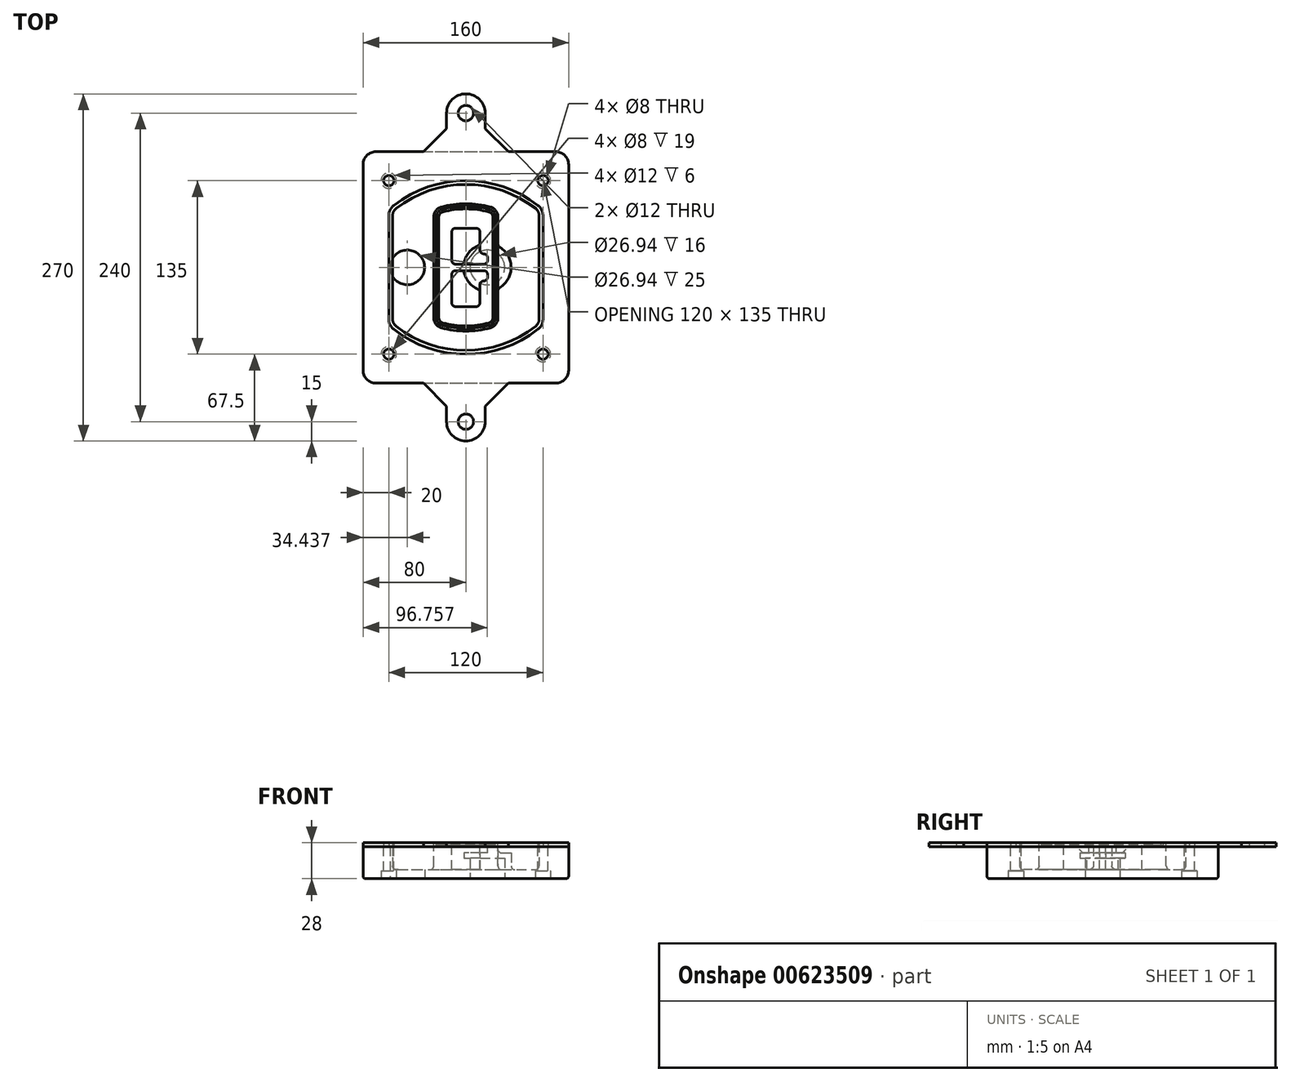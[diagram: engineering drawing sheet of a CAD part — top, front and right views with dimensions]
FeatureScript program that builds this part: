
annotation { "Feature Type Name" : "Feature", "Feature Type Description" : "" }
export const myFeature = defineFeature(function(context is Context, id is Id, definition is map)
    precondition{}
    {
        {
            var Q0;
            Q0=qCreatedBy(makeId("Top.planeOp"),FACE);
            var sketch = newSketch(context, id + "F0", { "sketchPlane" : qUnion([Q0])});
            skPoint(sketch, "E0.rect.middle", {"position": v(0, 0) * mm});
            skLineSegment(sketch, "E1.bottom", {"start": v(-70, -90) * mm, "end": v(70, -90) * mm});
            skLineSegment(sketch, "E1.top", {"start": v(-70, 90) * mm, "end": v(70, 90) * mm});
            skLineSegment(sketch, "E1.left", {"start": v(-80, -80) * mm, "end": v(-80, 80) * mm});
            skLineSegment(sketch, "E1.right", {"start": v(80, -80) * mm, "end": v(80, 80) * mm});
            skLineSegment(sketch, "E2", {"start": v(-80, 90) * mm, "end": v(80, -90) * mm, "construction": true});
            skLineSegment(sketch, "E3", {"start": v(80, 90) * mm, "end": v(-80, -90) * mm, "construction": true});
            skCircle(sketch, "E4", {"center": v(-60, 67.5) * mm, "radius": 4 * mm});
            skCircle(sketch, "E5", {"center": v(60, 67.5) * mm, "radius": 4 * mm});
            skCircle(sketch, "E6", {"center": v(60, -67.5) * mm, "radius": 4 * mm});
            skCircle(sketch, "E7", {"center": v(-60, -67.5) * mm, "radius": 4 * mm});
            skLineSegment(sketch, "E8", {"start": v(-60, 67.5) * mm, "end": v(60, 67.5) * mm, "construction": true});
            skLineSegment(sketch, "E9", {"start": v(60, 67.5) * mm, "end": v(60, -67.5) * mm, "construction": true});
            skLineSegment(sketch, "E10", {"start": v(60, -67.5) * mm, "end": v(-60, -67.5) * mm, "construction": true});
            skLineSegment(sketch, "E11", {"start": v(-60, -67.5) * mm, "end": v(-60, 67.5) * mm, "construction": true});
            skLineSegment(sketch, "E12", {"start": v(-60, 40.3) * mm, "end": v(-60, -40.3) * mm});
            skLineSegment(sketch, "E13", {"start": v(60, 40.3) * mm, "end": v(60, -40.3) * mm});
            skArc(sketch, "E14", {"start": v(56.15, 48.18) * mm, "mid": v(0, 67.5) * mm, "end": v(-56.15, 48.18) * mm});
            skArc(sketch, "E15", {"start": v(-56.15, -48.18) * mm, "mid": v(0, -67.5) * mm, "end": v(56.15, -48.18) * mm});
            skLineSegment(sketch, "E16", {"start": v(-60, 0) * mm, "end": v(60, 0) * mm, "construction": true});
            skPoint(sketch, "E17.visualSharp", {"position": v(-60, -45) * mm});
            skArc(sketch, "E17.filletArc", {"start": v(-60, -40.3) * mm, "mid": v(-58.99, -44.68) * mm, "end": v(-56.15, -48.18) * mm});
            skPoint(sketch, "E18.visualSharp", {"position": v(-60, 45) * mm});
            skArc(sketch, "E18.filletArc", {"start": v(-56.15, 48.18) * mm, "mid": v(-58.99, 44.68) * mm, "end": v(-60, 40.3) * mm});
            skPoint(sketch, "E19.visualSharp", {"position": v(60, 45) * mm});
            skArc(sketch, "E19.filletArc", {"start": v(60, 40.3) * mm, "mid": v(58.99, 44.68) * mm, "end": v(56.15, 48.18) * mm});
            skPoint(sketch, "E20.visualSharp", {"position": v(60, -45) * mm});
            skArc(sketch, "E20.filletArc", {"start": v(56.15, -48.18) * mm, "mid": v(58.99, -44.68) * mm, "end": v(60, -40.3) * mm});
            skPoint(sketch, "E21.visualSharp", {"position": v(-80, 90) * mm});
            skArc(sketch, "E21.filletArc", {"start": v(-70, 90) * mm, "mid": v(-77.07, 87.07) * mm, "end": v(-80, 80) * mm});
            skPoint(sketch, "E22.visualSharp", {"position": v(80, 90) * mm});
            skArc(sketch, "E22.filletArc", {"start": v(80, 80) * mm, "mid": v(77.07, 87.07) * mm, "end": v(70, 90) * mm});
            skPoint(sketch, "E23.visualSharp", {"position": v(80, -90) * mm});
            skArc(sketch, "E23.filletArc", {"start": v(70, -90) * mm, "mid": v(77.07, -87.07) * mm, "end": v(80, -80) * mm});
            skPoint(sketch, "E24.visualSharp", {"position": v(-80, -90) * mm});
            skArc(sketch, "E24.filletArc", {"start": v(-80, -80) * mm, "mid": v(-77.07, -87.07) * mm, "end": v(-70, -90) * mm});
            skArc(sketch, "E25.0", {"start": v(57, 40.3) * mm, "mid": v(56.3, 43.36) * mm, "end": v(54.3, 45.81) * mm});
            skLineSegment(sketch, "E25.1", {"start": v(57, 40.3) * mm, "end": v(57, -40.3) * mm});
            skArc(sketch, "E25.2", {"start": v(54.3, -45.81) * mm, "mid": v(56.3, -43.36) * mm, "end": v(57, -40.3) * mm});
            skArc(sketch, "E25.3", {"start": v(-54.3, -45.81) * mm, "mid": v(0, -64.5) * mm, "end": v(54.3, -45.81) * mm});
            skArc(sketch, "E25.4", {"start": v(-57, -40.3) * mm, "mid": v(-56.3, -43.36) * mm, "end": v(-54.3, -45.81) * mm});
            skArc(sketch, "E25.5", {"start": v(54.3, 45.81) * mm, "mid": v(0, 64.5) * mm, "end": v(-54.3, 45.81) * mm});
            skLineSegment(sketch, "E25.6", {"start": v(-57, 40.3) * mm, "end": v(-57, -40.3) * mm});
            skArc(sketch, "E25.7", {"start": v(-54.3, 45.81) * mm, "mid": v(-56.3, 43.36) * mm, "end": v(-57, 40.3) * mm});
            skArc(sketch, "E26.0", {"start": v(-58.62, 51.33) * mm, "mid": v(-62.58, 46.43) * mm, "end": v(-64, 40.3) * mm});
            skArc(sketch, "E26.1", {"start": v(58.62, 51.33) * mm, "mid": v(0, 71.5) * mm, "end": v(-58.62, 51.33) * mm});
            skArc(sketch, "E26.2", {"start": v(64, 40.3) * mm, "mid": v(62.58, 46.43) * mm, "end": v(58.62, 51.33) * mm});
            skLineSegment(sketch, "E26.3", {"start": v(64, 40.3) * mm, "end": v(64, -40.3) * mm});
            skArc(sketch, "E26.4", {"start": v(58.62, -51.33) * mm, "mid": v(62.58, -46.43) * mm, "end": v(64, -40.3) * mm});
            skLineSegment(sketch, "E26.5", {"start": v(-64, 40.3) * mm, "end": v(-64, -40.3) * mm});
            skArc(sketch, "E26.6", {"start": v(-58.62, -51.33) * mm, "mid": v(0, -71.5) * mm, "end": v(58.62, -51.33) * mm});
            skArc(sketch, "E26.7", {"start": v(-64, -40.3) * mm, "mid": v(-62.58, -46.43) * mm, "end": v(-58.62, -51.33) * mm});
            skSolve(sketch);
        }
        {
            var Q0;
            Q0=makeQuery(id+"F0.imprint","IMPRINT",FACE,{"disambiguationData":[TD([[makeQuery(id+"F0.imprint","IMPRINT",EDGE,{"derivedFrom":sQuery(id+"F0.wireOp",EDGE,"E1.bottom")}),1.0]])]});
            var Q1;
            Q1=makeQuery(id+"F0.imprint","IMPRINT",FACE,{"disambiguationData":[TD([[makeQuery(id+"F0.imprint","IMPRINT",EDGE,{"derivedFrom":sQuery(id+"F0.wireOp",EDGE,"E12")}),1.0]])]});
            var Q2;
            Q2=makeQuery(id+"F0.imprint","IMPRINT",FACE,{"disambiguationData":[TD([[makeQuery(id+"F0.imprint","IMPRINT",EDGE,{"derivedFrom":sQuery(id+"F0.wireOp",EDGE,"E25.0")}),1.0]])]});
            var Q3;
            Q3=makeQuery(id+"F0.imprint","IMPRINT",FACE,{"disambiguationData":[TD([[makeQuery(id+"F0.imprint","IMPRINT",EDGE,{"derivedFrom":sQuery(id+"F0.wireOp",EDGE,"E12")}),-1.0]])]});
            extrude(context, id + "F1", {"entities" : qUnion([Q0, Q1, Q2, Q3]), "oppositeDirection" : true, "depth" : 25 * mm});
        }
        {
            var Q0;
            Q0=makeQuery(id+"F0.imprint","IMPRINT",FACE,{"disambiguationData":[TD([[makeQuery(id+"F0.imprint","IMPRINT",EDGE,{"derivedFrom":sQuery(id+"F0.wireOp",EDGE,"E12")}),1.0]])]});
            extrude(context, id + "F2", {"entities" : qUnion([Q0]), "operationType" : NewBodyOperationType.ADD, "depth" : 3 * mm});
        }
        {
            var Q0;
            Q0=makeQuery(id+"F0.imprint","IMPRINT",FACE,{"disambiguationData":[TD([[makeQuery(id+"F0.imprint","IMPRINT",EDGE,{"derivedFrom":sQuery(id+"F0.wireOp",EDGE,"E25.0")}),1.0]])]});
            extrude(context, id + "F3", {"entities" : qUnion([Q0]), "operationType" : NewBodyOperationType.REMOVE, "oppositeDirection" : true, "depth" : 18 * mm});
        }
        {
            var Q0;
            Q0=makeQuery(id+"F2.opExtrude","CAP_FACE",FACE,{"disambiguationData":[OSD([sQuery(id+"F0.wireOp",EDGE,"E12"),sQuery(id+"F0.wireOp",EDGE,"E13"),sQuery(id+"F0.wireOp",EDGE,"E14"),sQuery(id+"F0.wireOp",EDGE,"E15"),sQuery(id+"F0.wireOp",EDGE,"E17.filletArc"),sQuery(id+"F0.wireOp",EDGE,"E18.filletArc"),sQuery(id+"F0.wireOp",EDGE,"E19.filletArc"),sQuery(id+"F0.wireOp",EDGE,"E20.filletArc"),sQuery(id+"F0.wireOp",EDGE,"E25.0"),sQuery(id+"F0.wireOp",EDGE,"E25.1"),sQuery(id+"F0.wireOp",EDGE,"E25.2"),sQuery(id+"F0.wireOp",EDGE,"E25.3"),sQuery(id+"F0.wireOp",EDGE,"E25.4"),sQuery(id+"F0.wireOp",EDGE,"E25.5"),sQuery(id+"F0.wireOp",EDGE,"E25.6"),sQuery(id+"F0.wireOp",EDGE,"E25.7")])],"isStart":false});
            var sketch = newSketch(context, id + "F4", { "sketchPlane" : qUnion([Q0])});
            skArc(sketch, "E27.0", {"start": v(-19.08, -46.97) * mm, "mid": v(0, -49.5) * mm, "end": v(19.08, -46.97) * mm});
            skArc(sketch, "E28.0", {"start": v(19.08, 46.97) * mm, "mid": v(0, 49.5) * mm, "end": v(-19.08, 46.97) * mm});
            skLineSegment(sketch, "E29", {"start": v(-25, 39.25) * mm, "end": v(-25, -39.25) * mm});
            skLineSegment(sketch, "E30", {"start": v(25, 39.25) * mm, "end": v(25, -39.25) * mm});
            skLineSegment(sketch, "E31", {"start": v(-25, 45.1) * mm, "end": v(25, 45.1) * mm, "construction": true});
            skLineSegment(sketch, "E32", {"start": v(-25, -45.1) * mm, "end": v(25, -45.1) * mm, "construction": true});
            skPoint(sketch, "E33.visualSharp", {"position": v(-25, 45.1) * mm});
            skArc(sketch, "E33.filletArc", {"start": v(-19.08, 46.97) * mm, "mid": v(-23.35, 44.11) * mm, "end": v(-25, 39.25) * mm});
            skPoint(sketch, "E34.visualSharp", {"position": v(25, 45.1) * mm});
            skArc(sketch, "E34.filletArc", {"start": v(25, 39.25) * mm, "mid": v(23.35, 44.11) * mm, "end": v(19.08, 46.97) * mm});
            skPoint(sketch, "E35.visualSharp", {"position": v(25, -45.1) * mm});
            skArc(sketch, "E35.filletArc", {"start": v(19.08, -46.97) * mm, "mid": v(23.35, -44.11) * mm, "end": v(25, -39.25) * mm});
            skPoint(sketch, "E36.visualSharp", {"position": v(-25, -45.1) * mm});
            skArc(sketch, "E36.filletArc", {"start": v(-25, -39.25) * mm, "mid": v(-23.35, -44.11) * mm, "end": v(-19.08, -46.97) * mm});
            skArc(sketch, "E37.0", {"start": v(54.3, 45.81) * mm, "mid": v(0, 64.5) * mm, "end": v(-54.3, 45.81) * mm});
            skArc(sketch, "E37.1", {"start": v(-54.3, 45.81) * mm, "mid": v(-56.3, 43.36) * mm, "end": v(-57, 40.3) * mm});
            skLineSegment(sketch, "E37.2", {"start": v(-57, 40.3) * mm, "end": v(-57, -40.3) * mm});
            skArc(sketch, "E37.3", {"start": v(-57, -40.3) * mm, "mid": v(-56.3, -43.36) * mm, "end": v(-54.3, -45.81) * mm});
            skArc(sketch, "E37.4", {"start": v(-54.3, -45.81) * mm, "mid": v(0, -64.5) * mm, "end": v(54.3, -45.81) * mm});
            skArc(sketch, "E37.5", {"start": v(54.3, -45.81) * mm, "mid": v(56.3, -43.36) * mm, "end": v(57, -40.3) * mm});
            skLineSegment(sketch, "E37.6", {"start": v(57, 40.3) * mm, "end": v(57, -40.3) * mm});
            skArc(sketch, "E37.7", {"start": v(57, 40.3) * mm, "mid": v(56.3, 43.36) * mm, "end": v(54.3, 45.81) * mm});
            skLineSegment(sketch, "E38.0", {"start": v(23, 39.25) * mm, "end": v(23, -39.25) * mm});
            skArc(sketch, "E38.1", {"start": v(18.56, -45.04) * mm, "mid": v(21.76, -42.9) * mm, "end": v(23, -39.25) * mm});
            skArc(sketch, "E38.2", {"start": v(-18.56, -45.04) * mm, "mid": v(0, -47.5) * mm, "end": v(18.56, -45.04) * mm});
            skArc(sketch, "E38.3", {"start": v(-23, -39.25) * mm, "mid": v(-21.76, -42.9) * mm, "end": v(-18.56, -45.04) * mm});
            skLineSegment(sketch, "E38.4", {"start": v(-23, 39.25) * mm, "end": v(-23, -39.25) * mm});
            skArc(sketch, "E38.5", {"start": v(23, 39.25) * mm, "mid": v(21.76, 42.9) * mm, "end": v(18.56, 45.04) * mm});
            skArc(sketch, "E38.6", {"start": v(-18.56, 45.04) * mm, "mid": v(-21.76, 42.9) * mm, "end": v(-23, 39.25) * mm});
            skArc(sketch, "E38.7", {"start": v(18.56, 45.04) * mm, "mid": v(0, 47.5) * mm, "end": v(-18.56, 45.04) * mm});
            skArc(sketch, "E39.0", {"start": v(21, 39.25) * mm, "mid": v(20.18, 41.68) * mm, "end": v(18.04, 43.1) * mm});
            skLineSegment(sketch, "E39.1", {"start": v(21, 39.25) * mm, "end": v(21, -39.25) * mm});
            skArc(sketch, "E39.2", {"start": v(18.04, -43.1) * mm, "mid": v(20.18, -41.68) * mm, "end": v(21, -39.25) * mm});
            skArc(sketch, "E39.3", {"start": v(-18.04, -43.1) * mm, "mid": v(0, -45.5) * mm, "end": v(18.04, -43.1) * mm});
            skArc(sketch, "E39.4", {"start": v(-21, -39.25) * mm, "mid": v(-20.18, -41.68) * mm, "end": v(-18.04, -43.1) * mm});
            skArc(sketch, "E39.5", {"start": v(18.04, 43.1) * mm, "mid": v(0, 45.5) * mm, "end": v(-18.04, 43.1) * mm});
            skLineSegment(sketch, "E39.6", {"start": v(-21, 39.25) * mm, "end": v(-21, -39.25) * mm});
            skArc(sketch, "E39.7", {"start": v(-18.04, 43.1) * mm, "mid": v(-20.18, 41.68) * mm, "end": v(-21, 39.25) * mm});
            skLineSegment(sketch, "E40", {"start": v(-25, 0) * mm, "end": v(25, 0) * mm, "construction": true});
            skLineSegment(sketch, "E41", {"start": v(-11, 5.5) * mm, "end": v(-11, 27.5) * mm});
            skLineSegment(sketch, "E42", {"start": v(-8, 30.5) * mm, "end": v(8, 30.5) * mm});
            skLineSegment(sketch, "E43", {"start": v(11, 27.5) * mm, "end": v(11, 13.5) * mm});
            skLineSegment(sketch, "E44", {"start": v(14, 10.5) * mm, "end": v(14, 10.5) * mm});
            skLineSegment(sketch, "E45", {"start": v(17, 7.5) * mm, "end": v(17, 5.5) * mm});
            skLineSegment(sketch, "E46", {"start": v(14, 2.5) * mm, "end": v(-8, 2.5) * mm});
            skPoint(sketch, "E47.visualSharp", {"position": v(-11, 30.5) * mm});
            skArc(sketch, "E47.filletArc", {"start": v(-8, 30.5) * mm, "mid": v(-10.12, 29.62) * mm, "end": v(-11, 27.5) * mm});
            skPoint(sketch, "E48.visualSharp", {"position": v(11, 30.5) * mm});
            skArc(sketch, "E48.filletArc", {"start": v(11, 27.5) * mm, "mid": v(10.12, 29.62) * mm, "end": v(8, 30.5) * mm});
            skPoint(sketch, "E49.visualSharp", {"position": v(11, 10.5) * mm});
            skArc(sketch, "E49.filletArc", {"start": v(11, 13.5) * mm, "mid": v(11.88, 11.38) * mm, "end": v(14, 10.5) * mm});
            skPoint(sketch, "E50.visualSharp", {"position": v(17, 10.5) * mm});
            skArc(sketch, "E50.filletArc", {"start": v(17, 7.5) * mm, "mid": v(16.12, 9.62) * mm, "end": v(14, 10.5) * mm});
            skPoint(sketch, "E51.visualSharp", {"position": v(17, 2.5) * mm});
            skArc(sketch, "E51.filletArc", {"start": v(14, 2.5) * mm, "mid": v(16.12, 3.38) * mm, "end": v(17, 5.5) * mm});
            skPoint(sketch, "E52.visualSharp", {"position": v(-11, 2.5) * mm});
            skArc(sketch, "E52.filletArc", {"start": v(-11, 5.5) * mm, "mid": v(-10.12, 3.38) * mm, "end": v(-8, 2.5) * mm});
            skLineSegment(sketch, "E53.0.MirrorCS", {"start": v(14, -2.5) * mm, "end": v(-8, -2.5) * mm});
            skArc(sketch, "E54.0.MirrorCS", {"start": v(-11, -5.5) * mm, "mid": v(-10.12, -3.38) * mm, "end": v(-8, -2.5) * mm});
            skLineSegment(sketch, "E55.0.MirrorCS", {"start": v(-11, -5.5) * mm, "end": v(-11, -27.5) * mm});
            skArc(sketch, "E56.0.MirrorCS", {"start": v(-8, -30.5) * mm, "mid": v(-10.12, -29.62) * mm, "end": v(-11, -27.5) * mm});
            skLineSegment(sketch, "E57.0.MirrorCS", {"start": v(-8, -30.5) * mm, "end": v(8, -30.5) * mm});
            skArc(sketch, "E58.0.MirrorCS", {"start": v(11, -27.5) * mm, "mid": v(10.12, -29.62) * mm, "end": v(8, -30.5) * mm});
            skLineSegment(sketch, "E59.0.MirrorCS", {"start": v(11, -27.5) * mm, "end": v(11, -13.5) * mm});
            skArc(sketch, "E60.0.MirrorCS", {"start": v(11, -13.5) * mm, "mid": v(11.88, -11.38) * mm, "end": v(14, -10.5) * mm});
            skArc(sketch, "E61.0.MirrorCS", {"start": v(17, -7.5) * mm, "mid": v(16.12, -9.62) * mm, "end": v(14, -10.5) * mm});
            skLineSegment(sketch, "E62.0.MirrorCS", {"start": v(17, -7.5) * mm, "end": v(17, -5.5) * mm});
            skArc(sketch, "E63.0.MirrorCS", {"start": v(14, -2.5) * mm, "mid": v(16.12, -3.38) * mm, "end": v(17, -5.5) * mm});
            skSolve(sketch);
        }
        {
            var Q0;
            Q0=makeQuery(id+"F4.imprint","IMPRINT",FACE,{"disambiguationData":[TD([[makeQuery(id+"F4.imprint","IMPRINT",EDGE,{"derivedFrom":sQuery(id+"F4.wireOp",EDGE,"E27.0")}),1.0]])]});
            var Q1;
            Q1=makeQuery(id+"F4.imprint","IMPRINT",FACE,{"disambiguationData":[TD([[makeQuery(id+"F4.imprint","IMPRINT",EDGE,{"derivedFrom":sQuery(id+"F4.wireOp",EDGE,"E38.0")}),-1.0]])]});
            var Q2;
            Q2=makeQuery(id+"F4.imprint","IMPRINT",FACE,{"disambiguationData":[TD([[makeQuery(id+"F4.imprint","IMPRINT",EDGE,{"derivedFrom":sQuery(id+"F4.wireOp",EDGE,"E39.0")}),1.0]])]});
            extrude(context, id + "F5", {"entities" : qUnion([Q0, Q1, Q2]), "operationType" : NewBodyOperationType.ADD, "endBound" : BoundingType.UP_TO_NEXT, "oppositeDirection" : true, "depth" : 25 * mm});
        }
        {
            var Q0;
            Q0=makeQuery(id+"F4.imprint","IMPRINT",FACE,{"disambiguationData":[TD([[makeQuery(id+"F4.imprint","IMPRINT",EDGE,{"derivedFrom":sQuery(id+"F4.wireOp",EDGE,"E38.0")}),-1.0]])]});
            extrude(context, id + "F6", {"entities" : qUnion([Q0]), "operationType" : NewBodyOperationType.REMOVE, "oppositeDirection" : true, "depth" : 2 * mm});
        }
        {
            var Q0;
            Q0=makeQuery(id+"F1.opExtrude","CAP_FACE",FACE,{"disambiguationData":[OSD([sQuery(id+"F0.wireOp",EDGE,"E1.bottom"),sQuery(id+"F0.wireOp",EDGE,"E1.top"),sQuery(id+"F0.wireOp",EDGE,"E1.left"),sQuery(id+"F0.wireOp",EDGE,"E1.right"),sQuery(id+"F0.wireOp",EDGE,"E4"),sQuery(id+"F0.wireOp",EDGE,"E5"),sQuery(id+"F0.wireOp",EDGE,"E6"),sQuery(id+"F0.wireOp",EDGE,"E7"),sQuery(id+"F0.wireOp",EDGE,"E21.filletArc"),sQuery(id+"F0.wireOp",EDGE,"E22.filletArc"),sQuery(id+"F0.wireOp",EDGE,"E23.filletArc"),sQuery(id+"F0.wireOp",EDGE,"E24.filletArc")])],"isStart":false});
            var sketch = newSketch(context, id + "F7", { "sketchPlane" : qUnion([Q0])});
            skCircle(sketch, "E64", {"center": v(16.76, 0) * mm, "radius": 13.47 * mm});
            skCircle(sketch, "E65", {"center": v(-45.56, 0) * mm, "radius": 13.47 * mm});
            skLineSegment(sketch, "E66", {"start": v(80, 0) * mm, "end": v(-80, 0) * mm});
            skCircle(sketch, "E67", {"center": v(16.76, 0) * mm, "radius": 18.47 * mm});
            skCircle(sketch, "E68", {"center": v(60, -67.5) * mm, "radius": 6 * mm});
            skCircle(sketch, "E69", {"center": v(-60, -67.5) * mm, "radius": 6 * mm});
            skCircle(sketch, "E70", {"center": v(-60, 67.5) * mm, "radius": 6 * mm});
            skCircle(sketch, "E71", {"center": v(60, 67.5) * mm, "radius": 6 * mm});
            skSolve(sketch);
        }
        {
            var Q0;
            {var subQ1=sQuery(id+"F7.wireOp",EDGE,"E66");var subQ4=sQuery(id+"F7.wireOp",EDGE,"E64");var subQ6=makeQuery(id+"F7.imprint","INTERSECT",VERTEX,{"disambiguationData":[OD(0.0)],"derivedFrom":[subQ4,subQ1]});Q0=makeQuery(id+"F7.imprint","IMPRINT",FACE,{"disambiguationData":[TD([[makeQuery(id+"F7.imprint","IMPRINT",EDGE,{"disambiguationData":[TD([[subQ6,-1.0]])],"derivedFrom":subQ4}),-1.0]])]});}
            var Q1;
            {var subQ0=sQuery(id+"F7.wireOp",EDGE,"E66");var subQ1=sQuery(id+"F7.wireOp",EDGE,"E64");var subQ3=makeQuery(id+"F7.imprint","INTERSECT",VERTEX,{"disambiguationData":[OD(0.0)],"derivedFrom":[subQ1,subQ0]});Q1=makeQuery(id+"F7.imprint","IMPRINT",FACE,{"disambiguationData":[TD([[makeQuery(id+"F7.imprint","IMPRINT",EDGE,{"disambiguationData":[TD([[subQ3,-1.0]])],"derivedFrom":subQ1}),1.0]])]});}
            var Q2;
            {var subQ0=sQuery(id+"F7.wireOp",EDGE,"E66");var subQ1=sQuery(id+"F7.wireOp",EDGE,"E64");var subQ3=makeQuery(id+"F7.imprint","INTERSECT",VERTEX,{"disambiguationData":[OD(0.0)],"derivedFrom":[subQ1,subQ0]});Q2=makeQuery(id+"F7.imprint","IMPRINT",FACE,{"disambiguationData":[TD([[makeQuery(id+"F7.imprint","IMPRINT",EDGE,{"disambiguationData":[TD([[subQ3,1.0]])],"derivedFrom":subQ1}),1.0]])]});}
            var Q3;
            {var subQ1=sQuery(id+"F7.wireOp",EDGE,"E66");var subQ4=sQuery(id+"F7.wireOp",EDGE,"E64");var subQ6=makeQuery(id+"F7.imprint","INTERSECT",VERTEX,{"disambiguationData":[OD(0.0)],"derivedFrom":[subQ4,subQ1]});Q3=makeQuery(id+"F7.imprint","IMPRINT",FACE,{"disambiguationData":[TD([[makeQuery(id+"F7.imprint","IMPRINT",EDGE,{"disambiguationData":[TD([[subQ6,1.0]])],"derivedFrom":subQ4}),-1.0]])]});}
            extrude(context, id + "F8", {"entities" : qUnion([Q0, Q1, Q2, Q3]), "operationType" : NewBodyOperationType.ADD, "oppositeDirection" : true, "depth" : 20 * mm});
        }
        {
            var Q0;
            {var subQ0=sQuery(id+"F7.wireOp",EDGE,"E66");var subQ1=sQuery(id+"F7.wireOp",EDGE,"E64");var subQ3=makeQuery(id+"F7.imprint","INTERSECT",VERTEX,{"disambiguationData":[OD(0.0)],"derivedFrom":[subQ1,subQ0]});Q0=makeQuery(id+"F7.imprint","IMPRINT",FACE,{"disambiguationData":[TD([[makeQuery(id+"F7.imprint","IMPRINT",EDGE,{"disambiguationData":[TD([[subQ3,-1.0]])],"derivedFrom":subQ1}),1.0]])]});}
            var Q1;
            {var subQ0=sQuery(id+"F7.wireOp",EDGE,"E66");var subQ1=sQuery(id+"F7.wireOp",EDGE,"E64");var subQ3=makeQuery(id+"F7.imprint","INTERSECT",VERTEX,{"disambiguationData":[OD(0.0)],"derivedFrom":[subQ1,subQ0]});Q1=makeQuery(id+"F7.imprint","IMPRINT",FACE,{"disambiguationData":[TD([[makeQuery(id+"F7.imprint","IMPRINT",EDGE,{"disambiguationData":[TD([[subQ3,1.0]])],"derivedFrom":subQ1}),1.0]])]});}
            extrude(context, id + "F9", {"entities" : qUnion([Q0, Q1]), "operationType" : NewBodyOperationType.REMOVE, "oppositeDirection" : true, "depth" : 16 * mm});
        }
        {
            var Q0;
            {var subQ0=sQuery(id+"F7.wireOp",EDGE,"E66");var subQ1=sQuery(id+"F7.wireOp",EDGE,"E65");var subQ3=makeQuery(id+"F7.imprint","INTERSECT",VERTEX,{"disambiguationData":[OD(0.0)],"derivedFrom":[subQ1,subQ0]});Q0=makeQuery(id+"F7.imprint","IMPRINT",FACE,{"disambiguationData":[TD([[makeQuery(id+"F7.imprint","IMPRINT",EDGE,{"disambiguationData":[TD([[subQ3,-1.0]])],"derivedFrom":subQ1}),1.0]])]});}
            var Q1;
            {var subQ0=sQuery(id+"F7.wireOp",EDGE,"E66");var subQ1=sQuery(id+"F7.wireOp",EDGE,"E65");var subQ3=makeQuery(id+"F7.imprint","INTERSECT",VERTEX,{"disambiguationData":[OD(0.0)],"derivedFrom":[subQ1,subQ0]});Q1=makeQuery(id+"F7.imprint","IMPRINT",FACE,{"disambiguationData":[TD([[makeQuery(id+"F7.imprint","IMPRINT",EDGE,{"disambiguationData":[TD([[subQ3,1.0]])],"derivedFrom":subQ1}),1.0]])]});}
            extrude(context, id + "F10", {"entities" : qUnion([Q0, Q1]), "operationType" : NewBodyOperationType.REMOVE, "oppositeDirection" : true, "depth" : 25 * mm});
        }
        {
            var Q0;
            Q0=makeQuery(id+"F7.imprint","IMPRINT",FACE,{"disambiguationData":[TD([[makeQuery(id+"F7.imprint","IMPRINT",EDGE,{"derivedFrom":sQuery(id+"F7.wireOp",EDGE,"E68")}),1.0]])]});
            var Q1;
            Q1=makeQuery(id+"F7.imprint","IMPRINT",FACE,{"disambiguationData":[TD([[makeQuery(id+"F7.imprint","IMPRINT",EDGE,{"derivedFrom":makeQuery(id+"F1.opExtrude","CAP_EDGE",EDGE,{"disambiguationData":[OSD([sQuery(id+"F0.wireOp",EDGE,"E5")])],"isStart":false})}),-1.0]])]});
            var Q2;
            Q2=makeQuery(id+"F7.imprint","IMPRINT",FACE,{"disambiguationData":[TD([[makeQuery(id+"F7.imprint","IMPRINT",EDGE,{"derivedFrom":sQuery(id+"F7.wireOp",EDGE,"E69")}),1.0]])]});
            var Q3;
            Q3=makeQuery(id+"F7.imprint","IMPRINT",FACE,{"disambiguationData":[TD([[makeQuery(id+"F7.imprint","IMPRINT",EDGE,{"derivedFrom":makeQuery(id+"F1.opExtrude","CAP_EDGE",EDGE,{"disambiguationData":[OSD([sQuery(id+"F0.wireOp",EDGE,"E4")])],"isStart":false})}),-1.0]])]});
            var Q4;
            Q4=makeQuery(id+"F7.imprint","IMPRINT",FACE,{"disambiguationData":[TD([[makeQuery(id+"F7.imprint","IMPRINT",EDGE,{"derivedFrom":sQuery(id+"F7.wireOp",EDGE,"E70")}),1.0]])]});
            var Q5;
            Q5=makeQuery(id+"F7.imprint","IMPRINT",FACE,{"disambiguationData":[TD([[makeQuery(id+"F7.imprint","IMPRINT",EDGE,{"derivedFrom":makeQuery(id+"F1.opExtrude","CAP_EDGE",EDGE,{"disambiguationData":[OSD([sQuery(id+"F0.wireOp",EDGE,"E7")])],"isStart":false})}),-1.0]])]});
            var Q6;
            Q6=makeQuery(id+"F7.imprint","IMPRINT",FACE,{"disambiguationData":[TD([[makeQuery(id+"F7.imprint","IMPRINT",EDGE,{"derivedFrom":sQuery(id+"F7.wireOp",EDGE,"E71")}),1.0]])]});
            var Q7;
            Q7=makeQuery(id+"F7.imprint","IMPRINT",FACE,{"disambiguationData":[TD([[makeQuery(id+"F7.imprint","IMPRINT",EDGE,{"derivedFrom":makeQuery(id+"F1.opExtrude","CAP_EDGE",EDGE,{"disambiguationData":[OSD([sQuery(id+"F0.wireOp",EDGE,"E6")])],"isStart":false})}),-1.0]])]});
            extrude(context, id + "F11", {"entities" : qUnion([Q0, Q1, Q2, Q3, Q4, Q5, Q6, Q7]), "operationType" : NewBodyOperationType.REMOVE, "oppositeDirection" : true, "depth" : 6 * mm});
        }
        {
            var Q0;
            Q0=makeQuery(id+"F9.boolean.opBoolean","COPY",FACE,{"derivedFrom":makeQuery(id+"F9.opExtrude","CAP_FACE",FACE,{"disambiguationData":[OSD([sQuery(id+"F7.wireOp",EDGE,"E64")])],"isStart":false})});
            var sketch = newSketch(context, id + "F12", { "sketchPlane" : qUnion([Q0])});
            skArc(sketch, "E72.0", {"start": v(11, 17.55) * mm, "mid": v(2.57, 11.82) * mm, "end": v(-1.54, 2.5) * mm});
            skArc(sketch, "E72.1", {"start": v(-1.54, -2.5) * mm, "mid": v(2.57, -11.82) * mm, "end": v(11, -17.55) * mm});
            skLineSegment(sketch, "E73", {"start": v(-1.54, -2.5) * mm, "end": v(14, -2.5) * mm});
            skLineSegment(sketch, "E74.0", {"start": v(14, 2.5) * mm, "end": v(-1.54, 2.5) * mm});
            skArc(sketch, "E74.1", {"start": v(14, 2.5) * mm, "mid": v(16.12, 3.38) * mm, "end": v(17, 5.5) * mm});
            skLineSegment(sketch, "E74.2", {"start": v(17, 7.5) * mm, "end": v(17, 5.5) * mm});
            skArc(sketch, "E74.3", {"start": v(17, 7.5) * mm, "mid": v(16.12, 9.62) * mm, "end": v(14, 10.5) * mm});
            skArc(sketch, "E74.4", {"start": v(11, 13.5) * mm, "mid": v(11.88, 11.38) * mm, "end": v(14, 10.5) * mm});
            skLineSegment(sketch, "E74.5", {"start": v(11, 17.55) * mm, "end": v(11, 13.5) * mm});
            skLineSegment(sketch, "E74.7", {"start": v(14, -2.5) * mm, "end": v(-1.54, -2.5) * mm});
            skArc(sketch, "E74.8", {"start": v(14, -2.5) * mm, "mid": v(16.12, -3.38) * mm, "end": v(17, -5.5) * mm});
            skLineSegment(sketch, "E74.9", {"start": v(17, -7.5) * mm, "end": v(17, -5.5) * mm});
            skArc(sketch, "E74.10", {"start": v(17, -7.5) * mm, "mid": v(16.12, -9.62) * mm, "end": v(14, -10.5) * mm});
            skArc(sketch, "E74.11", {"start": v(11, -13.5) * mm, "mid": v(11.88, -11.38) * mm, "end": v(14, -10.5) * mm});
            skLineSegment(sketch, "E74.12", {"start": v(11, -17.55) * mm, "end": v(11, -13.5) * mm});
            skPoint(sketch, "E75.orphan", {"position": v(11, -27.5) * mm});
            skPoint(sketch, "E76.orphan", {"position": v(-8, -2.5) * mm});
            skPoint(sketch, "E77.orphan", {"position": v(-8, 2.5) * mm});
            skPoint(sketch, "E78.orphan", {"position": v(11, 27.5) * mm});
            skSolve(sketch);
        }
        {
            var Q0;
            {var subQ7=sQuery(id+"F12.wireOp",EDGE,"E72.0");var subQ14=sQuery(id+"F12.wireOp",EDGE,"E72.1");var subQ16=sQuery(id+"F12.wireOp",EDGE,"E74.1");var subQ18=sQuery(id+"F12.wireOp",EDGE,"E74.8");Q0=qUnion([makeQuery(id+"F12.imprint","IMPRINT",FACE,{"disambiguationData":[TD([[makeQuery(id+"F12.imprint","IMPRINT",EDGE,{"derivedFrom":subQ7}),1.0]])]}),makeQuery(id+"F12.imprint","IMPRINT",FACE,{"disambiguationData":[TD([[makeQuery(id+"F12.imprint","IMPRINT",EDGE,{"derivedFrom":subQ14}),1.0]])]}),makeQuery(id+"F12.imprint","IMPRINT",FACE,{"disambiguationData":[TD([[makeQuery(id+"F12.imprint","IMPRINT",EDGE,{"derivedFrom":subQ16}),1.0]])]}),makeQuery(id+"F12.imprint","IMPRINT",FACE,{"disambiguationData":[TD([[makeQuery(id+"F12.imprint","IMPRINT",EDGE,{"derivedFrom":subQ18}),-1.0]])]})]);}
            var Q1;
            Q1=makeQuery(id+"F5.boolean.opBoolean","SPLIT",FACE,{"disambiguationData":[TD([makeQuery(id+"F5.opExtrude","SWEPT_FACE",FACE,{"disambiguationData":[OSD([sQuery(id+"F4.wireOp",EDGE,"E41")])]})])],"derivedFrom":makeQuery(id+"F3.boolean.opBoolean","COPY",FACE,{"derivedFrom":makeQuery(id+"F3.opExtrude","CAP_FACE",FACE,{"disambiguationData":[OSD([sQuery(id+"F0.wireOp",EDGE,"E25.0"),sQuery(id+"F0.wireOp",EDGE,"E25.1"),sQuery(id+"F0.wireOp",EDGE,"E25.2"),sQuery(id+"F0.wireOp",EDGE,"E25.3"),sQuery(id+"F0.wireOp",EDGE,"E25.4"),sQuery(id+"F0.wireOp",EDGE,"E25.5"),sQuery(id+"F0.wireOp",EDGE,"E25.6"),sQuery(id+"F0.wireOp",EDGE,"E25.7")])],"isStart":false})})});
            extrude(context, id + "F13", {"entities" : qUnion([Q0]), "operationType" : NewBodyOperationType.REMOVE, "endBound" : BoundingType.UP_TO_SURFACE, "endBoundEntityFace" : qUnion([Q1]), "depth" : 25 * mm});
        }
        {
            var Q0;
            Q0=makeQuery(id+"F3.boolean.opBoolean","COPY",EDGE,{"derivedFrom":makeQuery(id+"F3.opExtrude","CAP_EDGE",EDGE,{"disambiguationData":[OSD([sQuery(id+"F0.wireOp",EDGE,"E25.6")])],"isStart":false})});
            var Q1;
            Q1=makeQuery(id+"F8.boolean.opBoolean","INTERSECT",EDGE,{"derivedFrom":[makeQuery(id+"F5.opExtrude","SWEPT_FACE",FACE,{"disambiguationData":[OSD([sQuery(id+"F4.wireOp",EDGE,"E30")])]}),makeQuery(id+"F8.opExtrude","CAP_FACE",FACE,{"disambiguationData":[OSD([sQuery(id+"F7.wireOp",EDGE,"E67")])],"isStart":false})]});
            var Q2;
            Q2=makeQuery(id+"F8.boolean.opBoolean","INTERSECT",EDGE,{"disambiguationData":[OD(1.0)],"derivedFrom":[makeQuery(id+"F5.opExtrude","SWEPT_FACE",FACE,{"disambiguationData":[OSD([sQuery(id+"F4.wireOp",EDGE,"E30")])]}),makeQuery(id+"F8.opExtrude","SWEPT_FACE",FACE,{"disambiguationData":[OSD([sQuery(id+"F7.wireOp",EDGE,"E67")])]})]});
            var Q3;
            {var subQ0=sQuery(id+"F4.wireOp",EDGE,"E30");Q3=makeQuery(id+"F8.boolean.opBoolean","SPLIT",EDGE,{"disambiguationData":[TD([makeQuery(id+"F5.opExtrude","SWEPT_FACE",FACE,{"disambiguationData":[OSD([sQuery(id+"F4.wireOp",EDGE,"E35.filletArc")])]})])],"derivedFrom":makeQuery(id+"F5.opExtrude","CAP_EDGE",EDGE,{"disambiguationData":[OSD([subQ0])],"isStart":false})});}
            var Q4;
            {var subQ0=sQuery(id+"F0.wireOp",EDGE,"E25.7");var subQ1=sQuery(id+"F0.wireOp",EDGE,"E25.1");var subQ2=sQuery(id+"F0.wireOp",EDGE,"E25.6");var subQ3=sQuery(id+"F0.wireOp",EDGE,"E25.5");var subQ4=sQuery(id+"F0.wireOp",EDGE,"E25.4");var subQ5=sQuery(id+"F0.wireOp",EDGE,"E25.0");var subQ6=sQuery(id+"F0.wireOp",EDGE,"E25.2");var subQ7=sQuery(id+"F0.wireOp",EDGE,"E25.3");Q4=makeQuery(id+"F8.boolean.opBoolean","INTERSECT",EDGE,{"derivedFrom":[makeQuery(id+"F5.boolean.opBoolean","SPLIT",FACE,{"disambiguationData":[TD([makeQuery(id+"F2.opExtrude","SWEPT_FACE",FACE,{"disambiguationData":[OSD([subQ5])]})])],"derivedFrom":makeQuery(id+"F3.boolean.opBoolean","COPY",FACE,{"derivedFrom":makeQuery(id+"F3.opExtrude","CAP_FACE",FACE,{"disambiguationData":[OSD([subQ5,subQ1,subQ6,subQ7,subQ4,subQ3,subQ2,subQ0])],"isStart":false})})}),makeQuery(id+"F8.opExtrude","SWEPT_FACE",FACE,{"disambiguationData":[OSD([sQuery(id+"F7.wireOp",EDGE,"E67")])]})]});}
            var Q5;
            Q5=makeQuery(id+"F8.boolean.opBoolean","INTERSECT",EDGE,{"disambiguationData":[OD(0.0)],"derivedFrom":[makeQuery(id+"F5.opExtrude","SWEPT_FACE",FACE,{"disambiguationData":[OSD([sQuery(id+"F4.wireOp",EDGE,"E30")])]}),makeQuery(id+"F8.opExtrude","SWEPT_FACE",FACE,{"disambiguationData":[OSD([sQuery(id+"F7.wireOp",EDGE,"E67")])]})]});
            fillet(context, id + "F14", {"entities" : qUnion([Q0, Q1, Q2, Q3, Q4, Q5]), "radius" : 3 * mm, "tangentPropagation" : true, "allowEdgeOverflow" : false});
        }
        {
            var Q0;
            Q0=makeQuery(id+"F1.opExtrude","CAP_EDGE",EDGE,{"disambiguationData":[OSD([sQuery(id+"F0.wireOp",EDGE,"E1.bottom")])],"isStart":false});
            fillet(context, id + "F15", {"entities" : qUnion([Q0]), "radius" : 2 * mm, "tangentPropagation" : true, "allowEdgeOverflow" : false});
        }
        {
            var Q0;
            {var subQ0=sQuery(id+"F0.wireOp",EDGE,"E21.filletArc");var subQ1=sQuery(id+"F0.wireOp",EDGE,"E7");var subQ2=sQuery(id+"F0.wireOp",EDGE,"E6");var subQ3=sQuery(id+"F0.wireOp",EDGE,"E5");var subQ4=sQuery(id+"F0.wireOp",EDGE,"E4");var subQ5=sQuery(id+"F0.wireOp",EDGE,"E22.filletArc");var subQ6=sQuery(id+"F0.wireOp",EDGE,"E1.bottom");var subQ7=sQuery(id+"F0.wireOp",EDGE,"E1.right");var subQ8=sQuery(id+"F0.wireOp",EDGE,"E1.top");var subQ9=sQuery(id+"F0.wireOp",EDGE,"E1.left");var subQ10=sQuery(id+"F0.wireOp",EDGE,"E23.filletArc");var subQ11=sQuery(id+"F0.wireOp",EDGE,"E24.filletArc");Q0=makeQuery(id+"F2.boolean.opBoolean","SPLIT",FACE,{"disambiguationData":[TD([makeQuery(id+"F1.opExtrude","SWEPT_FACE",FACE,{"disambiguationData":[OSD([subQ6])]})])],"derivedFrom":makeQuery(id+"F1.opExtrude","CAP_FACE",FACE,{"disambiguationData":[OSD([subQ6,subQ8,subQ9,subQ7,subQ4,subQ3,subQ2,subQ1,subQ0,subQ5,subQ10,subQ11])],"isStart":true})});}
            var sketch = newSketch(context, id + "F16", { "sketchPlane" : qUnion([Q0])});
            skArc(sketch, "E79.0", {"start": v(-70, 90) * mm, "mid": v(-77.07, 87.07) * mm, "end": v(-80, 80) * mm});
            skLineSegment(sketch, "E79.1", {"start": v(-70, 90) * mm, "end": v(70, 90) * mm});
            skArc(sketch, "E79.2", {"start": v(56.15, 48.18) * mm, "mid": v(0, 67.5) * mm, "end": v(-56.15, 48.18) * mm});
            skArc(sketch, "E79.3", {"start": v(-56.15, 48.18) * mm, "mid": v(-58.99, 44.68) * mm, "end": v(-60, 40.3) * mm});
            skLineSegment(sketch, "E79.4", {"start": v(-60, 40.3) * mm, "end": v(-60, -40.3) * mm});
            skLineSegment(sketch, "E79.5", {"start": v(-80, -80) * mm, "end": v(-80, 80) * mm});
            skCircle(sketch, "E79.6", {"center": v(-60, 67.5) * mm, "radius": 4 * mm});
            skCircle(sketch, "E79.7", {"center": v(-60, -67.5) * mm, "radius": 4 * mm});
            skPoint(sketch, "E79.8", {"position": v(-80, -80) * mm});
            skArc(sketch, "E79.9", {"start": v(-80, -80) * mm, "mid": v(-77.07, -87.07) * mm, "end": v(-70, -90) * mm});
            skArc(sketch, "E79.10", {"start": v(-60, -40.3) * mm, "mid": v(-58.99, -44.68) * mm, "end": v(-56.15, -48.18) * mm});
            skArc(sketch, "E79.11", {"start": v(-56.15, -48.18) * mm, "mid": v(0, -67.5) * mm, "end": v(56.15, -48.18) * mm});
            skLineSegment(sketch, "E79.12", {"start": v(-70, -90) * mm, "end": v(70, -90) * mm});
            skCircle(sketch, "E79.13", {"center": v(60, -67.5) * mm, "radius": 4 * mm});
            skArc(sketch, "E79.14", {"start": v(70, -90) * mm, "mid": v(77.07, -87.07) * mm, "end": v(80, -80) * mm});
            skLineSegment(sketch, "E79.15", {"start": v(80, -80) * mm, "end": v(80, 80) * mm});
            skArc(sketch, "E79.16", {"start": v(56.15, -48.18) * mm, "mid": v(58.99, -44.68) * mm, "end": v(60, -40.3) * mm});
            skLineSegment(sketch, "E79.17", {"start": v(60, 40.3) * mm, "end": v(60, -40.3) * mm});
            skArc(sketch, "E79.18", {"start": v(60, 40.3) * mm, "mid": v(58.99, 44.68) * mm, "end": v(56.15, 48.18) * mm});
            skArc(sketch, "E79.19", {"start": v(80, 80) * mm, "mid": v(77.07, 87.07) * mm, "end": v(70, 90) * mm});
            skCircle(sketch, "E79.20", {"center": v(60, 67.5) * mm, "radius": 4 * mm});
            skLineSegment(sketch, "E80", {"start": v(0, 90) * mm, "end": v(0, 120) * mm, "construction": true});
            skCircle(sketch, "E81", {"center": v(0, 120) * mm, "radius": 6 * mm});
            skArc(sketch, "E82", {"start": v(15, 120) * mm, "mid": v(0, 135) * mm, "end": v(-15, 120) * mm});
            skLineSegment(sketch, "E83", {"start": v(-15, 120) * mm, "end": v(-15, 108) * mm});
            skLineSegment(sketch, "E84", {"start": v(-15, 108) * mm, "end": v(-33, 90) * mm});
            skLineSegment(sketch, "E85.MirrorCS", {"start": v(15, 120) * mm, "end": v(15, 108) * mm});
            skLineSegment(sketch, "E86.MirrorCS", {"start": v(15, 108) * mm, "end": v(33, 90) * mm});
            skLineSegment(sketch, "E87", {"start": v(-80, 0) * mm, "end": v(80, 0) * mm, "construction": true});
            skLineSegment(sketch, "E88.MirrorCS", {"start": v(15, -108) * mm, "end": v(33, -90) * mm});
            skLineSegment(sketch, "E89.MirrorCS", {"start": v(15, -120) * mm, "end": v(15, -108) * mm});
            skCircle(sketch, "E90.MirrorC", {"center": v(0, -120) * mm, "radius": 6 * mm});
            skLineSegment(sketch, "E91.MirrorCS", {"start": v(-15, -120) * mm, "end": v(-15, -108) * mm});
            skArc(sketch, "E92.MirrorCS", {"start": v(15, -120) * mm, "mid": v(0, -135) * mm, "end": v(-15, -120) * mm});
            skLineSegment(sketch, "E93.MirrorCS", {"start": v(0, -90) * mm, "end": v(0, -120) * mm, "construction": true});
            skLineSegment(sketch, "E94.MirrorCS", {"start": v(-15, -108) * mm, "end": v(-33, -90) * mm});
            skSolve(sketch);
        }
        {
            var Q0;
            {var subQ9=sQuery(id+"F16.wireOp",EDGE,"E79.0");Q0=makeQuery(id+"F16.imprint","IMPRINT",FACE,{"disambiguationData":[TD([[makeQuery(id+"F16.imprint","IMPRINT",EDGE,{"derivedFrom":subQ9}),1.0]])]});}
            var Q1;
            Q1=makeQuery(id+"F16.imprint","IMPRINT",FACE,{"disambiguationData":[TD([[makeQuery(id+"F16.imprint","IMPRINT",EDGE,{"derivedFrom":sQuery(id+"F16.wireOp",EDGE,"E81")}),-1.0]])]});
            var Q2;
            {var subQ1=sQuery(id+"F16.wireOp",EDGE,"E88.MirrorCS");Q2=makeQuery(id+"F16.imprint","IMPRINT",FACE,{"disambiguationData":[TD([[makeQuery(id+"F16.imprint","IMPRINT",EDGE,{"derivedFrom":subQ1}),1.0]])]});}
            var Q3;
            Q3=makeQuery(id+"F2.opExtrude","CAP_FACE",FACE,{"disambiguationData":[OSD([sQuery(id+"F0.wireOp",EDGE,"E12"),sQuery(id+"F0.wireOp",EDGE,"E13"),sQuery(id+"F0.wireOp",EDGE,"E14"),sQuery(id+"F0.wireOp",EDGE,"E15"),sQuery(id+"F0.wireOp",EDGE,"E17.filletArc"),sQuery(id+"F0.wireOp",EDGE,"E18.filletArc"),sQuery(id+"F0.wireOp",EDGE,"E19.filletArc"),sQuery(id+"F0.wireOp",EDGE,"E20.filletArc"),sQuery(id+"F0.wireOp",EDGE,"E25.0"),sQuery(id+"F0.wireOp",EDGE,"E25.1"),sQuery(id+"F0.wireOp",EDGE,"E25.2"),sQuery(id+"F0.wireOp",EDGE,"E25.3"),sQuery(id+"F0.wireOp",EDGE,"E25.4"),sQuery(id+"F0.wireOp",EDGE,"E25.5"),sQuery(id+"F0.wireOp",EDGE,"E25.6"),sQuery(id+"F0.wireOp",EDGE,"E25.7")])],"isStart":false});
            extrude(context, id + "F17", {"entities" : qUnion([Q0, Q1, Q2]), "endBound" : BoundingType.UP_TO_SURFACE, "depth" : 25 * mm, "endBoundEntityFace" : qUnion([Q3]), "offsetDistance" : 25 * mm});
        }
    });
